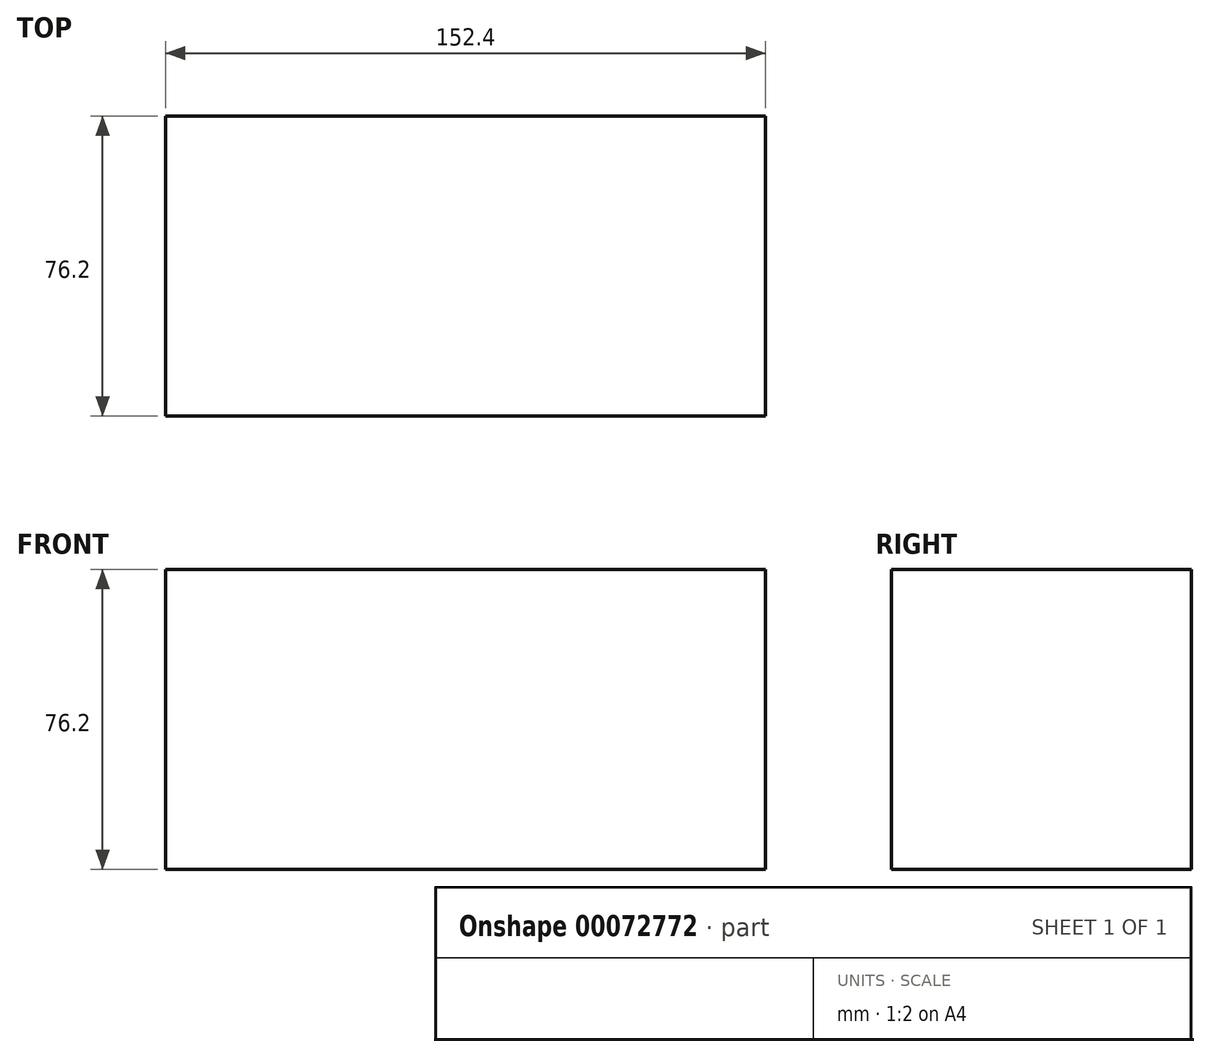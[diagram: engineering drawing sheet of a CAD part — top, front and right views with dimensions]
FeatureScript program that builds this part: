
annotation { "Feature Type Name" : "Feature", "Feature Type Description" : "" }
export const myFeature = defineFeature(function(context is Context, id is Id, definition is map)
    precondition{}
    {
        {
            var Q0;
            Q0=qCreatedBy(makeId("Top.planeOp"),FACE);
            var sketch = newSketch(context, id + "F0", { "sketchPlane" : qUnion([Q0])});
            skLineSegment(sketch, "E0.rect.bottom", {"start": v(76.2, -38.1) * mm, "end": v(-76.2, -38.1) * mm});
            skLineSegment(sketch, "E0.rect.top", {"start": v(76.2, 38.1) * mm, "end": v(-76.2, 38.1) * mm});
            skLineSegment(sketch, "E0.rect.left", {"start": v(76.2, -38.1) * mm, "end": v(76.2, 38.1) * mm});
            skLineSegment(sketch, "E0.rect.right", {"start": v(-76.2, -38.1) * mm, "end": v(-76.2, 38.1) * mm});
            skPoint(sketch, "E0.rect.middle", {"position": v(0, 0) * mm});
            skSolve(sketch);
        }
        {
            var Q0;
            Q0 = qSketchRegion(id + "F0", true);
            extrude(context, id + "F1", {"entities" : qUnion([Q0]), "depth" : 76.2 * mm});
        }
    });
